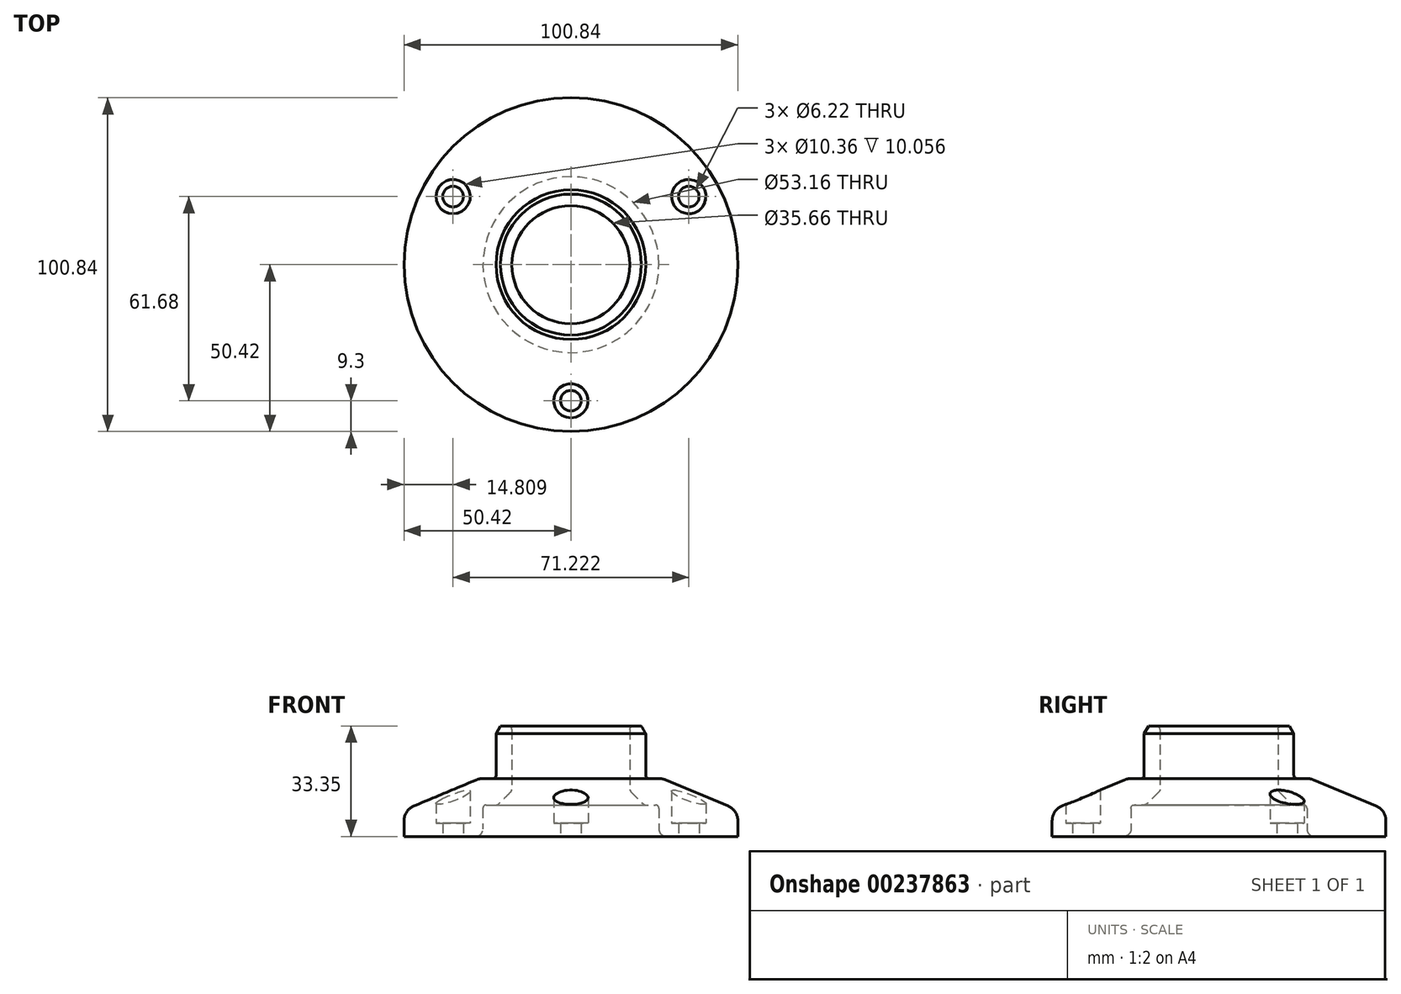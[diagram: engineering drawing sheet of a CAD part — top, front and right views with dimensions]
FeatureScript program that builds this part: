
annotation { "Feature Type Name" : "Feature", "Feature Type Description" : "" }
export const myFeature = defineFeature(function(context is Context, id is Id, definition is map)
    precondition{}
    {
        {
            var Q0;
            Q0=qCreatedBy(makeId("Front.planeOp"),FACE);
            var sketch = newSketch(context, id + "F0", { "sketchPlane" : qUnion([Q0])});
            skLineSegment(sketch, "E0", {"start": v(-28.87, 0) * mm, "end": v(-50.42, 0) * mm});
            skLineSegment(sketch, "E1", {"start": v(-26.58, 2.29) * mm, "end": v(-26.58, 8.5) * mm});
            skLineSegment(sketch, "E2", {"start": v(-25.57, 9.53) * mm, "end": v(-22.54, 9.53) * mm});
            skLineSegment(sketch, "E3", {"start": v(-50.42, 0) * mm, "end": v(-50.42, 4.77) * mm});
            skLineSegment(sketch, "E4", {"start": v(-22.6, 33.35) * mm, "end": v(-18.85, 33.35) * mm});
            skLineSegment(sketch, "E5", {"start": v(-17.83, 32.33) * mm, "end": v(-17.83, 14.24) * mm});
            skLineSegment(sketch, "E6", {"start": v(-21.82, 9.82) * mm, "end": v(-18.13, 13.52) * mm});
            skLineSegment(sketch, "E7", {"start": v(-22.6, 33.35) * mm, "end": v(-22.6, 18.5) * mm});
            skLineSegment(sketch, "E8", {"start": v(-23.62, 17.48) * mm, "end": v(-26.73, 17.48) * mm});
            skLineSegment(sketch, "E9", {"start": v(-28.57, 17.1) * mm, "end": v(-47.49, 9.18) * mm});
            skPoint(sketch, "E10.visualSharp", {"position": v(-50.42, 7.95) * mm});
            skArc(sketch, "E10.filletArc", {"start": v(-47.49, 9.18) * mm, "mid": v(-49.62, 7.42) * mm, "end": v(-50.42, 4.77) * mm});
            skPoint(sketch, "E11.visualSharp", {"position": v(-27.69, 17.48) * mm});
            skArc(sketch, "E11.filletArc", {"start": v(-26.73, 17.48) * mm, "mid": v(-27.67, 17.38) * mm, "end": v(-28.57, 17.1) * mm});
            skPoint(sketch, "E12.visualSharp", {"position": v(-17.83, 13.81) * mm});
            skArc(sketch, "E12.filletArc", {"start": v(-18.13, 13.52) * mm, "mid": v(-17.9, 13.85) * mm, "end": v(-17.83, 14.24) * mm});
            skPoint(sketch, "E13.visualSharp", {"position": v(-22.12, 9.53) * mm});
            skArc(sketch, "E13.filletArc", {"start": v(-22.54, 9.53) * mm, "mid": v(-22.15, 9.6) * mm, "end": v(-21.82, 9.82) * mm});
            skPoint(sketch, "E14.visualSharp", {"position": v(-22.6, 17.48) * mm});
            skArc(sketch, "E14.filletArc", {"start": v(-23.62, 17.48) * mm, "mid": v(-22.9, 17.77) * mm, "end": v(-22.6, 18.5) * mm});
            skPoint(sketch, "E15.visualSharp", {"position": v(-17.83, 33.35) * mm});
            skArc(sketch, "E15.filletArc", {"start": v(-17.83, 32.33) * mm, "mid": v(-18.13, 33.05) * mm, "end": v(-18.85, 33.35) * mm});
            skPoint(sketch, "E16.visualSharp", {"position": v(-26.58, 0) * mm});
            skArc(sketch, "E16.filletArc", {"start": v(-28.87, 0) * mm, "mid": v(-27.25, 0.67) * mm, "end": v(-26.58, 2.29) * mm});
            skPoint(sketch, "E17.visualSharp", {"position": v(-26.58, 9.52) * mm});
            skArc(sketch, "E17.filletArc", {"start": v(-25.57, 9.53) * mm, "mid": v(-26.28, 9.23) * mm, "end": v(-26.58, 8.5) * mm});
            skSolve(sketch);
        }
        {
            var Q0;
            Q0=qCreatedBy(makeId("Front.planeOp"),FACE);
            var sketch = newSketch(context, id + "F1", { "sketchPlane" : qUnion([Q0])});
            skLineSegment(sketch, "E18", {"start": v(0, 0) * mm, "end": v(0, 33.35) * mm});
            skSolve(sketch);
        }
        {
            var Q0;
            Q0=makeQuery(id+"F0.imprint","IMPRINT",FACE,{"disambiguationData":[TD([[makeQuery(id+"F0.imprint","IMPRINT",EDGE,{"derivedFrom":sQuery(id+"F0.wireOp",EDGE,"E0")}),-1.0]])]});
            var Q1;
            Q1=sQuery(id+"F1.wireOp",EDGE,"E18");
            revolve(context, id + "F2", {"entities" : qUnion([Q0]), "axis" : qUnion([Q1]), "revolveType" : RevolveType.FULL});
        }
        {
            var Q0;
            Q0=makeQuery(id+"F2.opRevolve","SWEPT_EDGE",EDGE,{"disambiguationData":[OSD([sQuery(id+"F0.wireOp",EDGE,"E4"),sQuery(id+"F0.wireOp",EDGE,"E7")])]});
            chamfer(context, id + "F3", {"entities" : qUnion([Q0]), "chamferType" : ChamferType.OFFSET_ANGLE, "width" : 2.3 * mm, "oppositeDirection" : false, "angle" : 30 * degree, "tangentPropagation" : true});
        }
        {
            var Q0;
            Q0=makeQuery(id+"F2.opRevolve","SWEPT_FACE",FACE,{"disambiguationData":[OSD([sQuery(id+"F0.wireOp",EDGE,"E0")])]});
            var sketch = newSketch(context, id + "F4", { "sketchPlane" : qUnion([Q0])});
            skCircle(sketch, "E19", {"center": v(0, 41.12) * mm, "radius": 3.11 * mm});
            skCircle(sketch, "E20", {"center": v(-35.61, -20.56) * mm, "radius": 3.11 * mm});
            skCircle(sketch, "E21", {"center": v(35.61, -20.56) * mm, "radius": 3.11 * mm});
            skCircle(sketch, "E22", {"center": v(0, 0) * mm, "radius": 41.12 * mm, "construction": true});
            skSolve(sketch);
        }
        {
            var Q0;
            Q0=makeQuery(id+"F4.imprint","IMPRINT",FACE,{"disambiguationData":[TD([[makeQuery(id+"F4.imprint","IMPRINT",EDGE,{"derivedFrom":sQuery(id+"F4.wireOp",EDGE,"E21")}),1.0]])]});
            var Q1;
            Q1=makeQuery(id+"F4.imprint","IMPRINT",FACE,{"disambiguationData":[TD([[makeQuery(id+"F4.imprint","IMPRINT",EDGE,{"derivedFrom":sQuery(id+"F4.wireOp",EDGE,"E20")}),1.0]])]});
            var Q2;
            Q2=makeQuery(id+"F4.imprint","IMPRINT",FACE,{"disambiguationData":[TD([[makeQuery(id+"F4.imprint","IMPRINT",EDGE,{"derivedFrom":sQuery(id+"F4.wireOp",EDGE,"E19")}),1.0]])]});
            extrude(context, id + "F5", {"entities" : qUnion([Q0, Q1, Q2]), "operationType" : NewBodyOperationType.REMOVE, "endBound" : BoundingType.THROUGH_ALL, "oppositeDirection" : true, "depth" : 25.4 * mm});
        }
        {
            var Q0;
            Q0=qCreatedBy(makeId("Top.planeOp"),FACE);
            cPlane(context, id + "F6", {"entities" : qUnion([Q0]), "cplaneType" : CPlaneType.OFFSET, "offset" : 3.96 * mm, "width" : 152.4 * mm, "height" : 152.4 * mm});
        }
        {
            var Q0;
            Q0=qCreatedBy(id+"F6.planeOp",FACE);
            var sketch = newSketch(context, id + "F7", { "sketchPlane" : qUnion([Q0])});
            skCircle(sketch, "E23", {"center": v(0, -41.12) * mm, "radius": 5.18 * mm});
            skCircle(sketch, "E24", {"center": v(35.61, 20.56) * mm, "radius": 5.18 * mm});
            skCircle(sketch, "E25", {"center": v(-35.61, 20.56) * mm, "radius": 5.18 * mm});
            skSolve(sketch);
        }
        {
            var Q0;
            Q0 = qSketchRegion(id + "F7", true);
            extrude(context, id + "F8", {"entities" : qUnion([Q0]), "operationType" : NewBodyOperationType.REMOVE, "endBound" : BoundingType.THROUGH_ALL, "depth" : 25.4 * mm});
        }
    });
